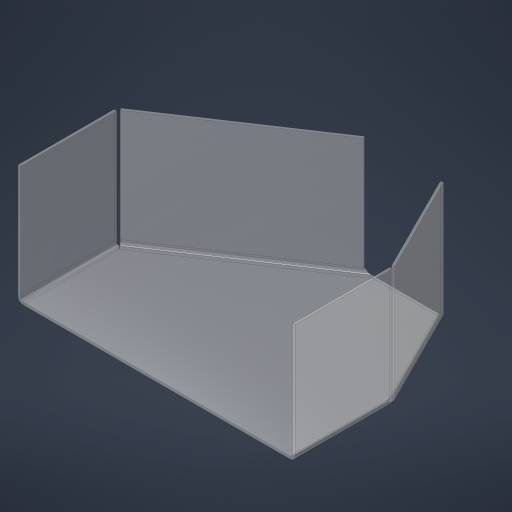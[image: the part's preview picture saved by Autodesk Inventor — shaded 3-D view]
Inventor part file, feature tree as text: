
AUTODESK INVENTOR PART (.ipt)
format: ipt  version: 2023.4 (Build 274418000, 418)  size: 233,472 bytes
history: native  units: in
note: dims shown in document units (in); Inventor stores cm internally (conversion verified against a paired STEP export)
features: sheet_metal_op x4, sketch x2, other x2
ambient origin geometry x8: Origin, YZ Plane, XZ Plane, XY Plane, X Axis, Y Axis, Z Axis, Center Point
bodies: Solid1 (feature_tree)
feature tree (8):
  sheet_metal_op  "Face1"
  sheet_metal_op  "Flange1"
  sketch  "Sketch1"  dims[d0=14.0in]
  other  "Plate1"
  sketch  "Sketch2"  dims[d1=10.0in d2=0.125in d4=5.0in d5=0.125in d6=0.0625in d7=0.25in d8=0.125in d9=6.0in d10=90.0deg d11=0.125in d12=0.5in d13=0.125in d14=0.125in d15=4.0in d16=2.5in]
  other  "Plate2"
  sheet_metal_op  "Bend1"
  sheet_metal_op  "Corner1"
